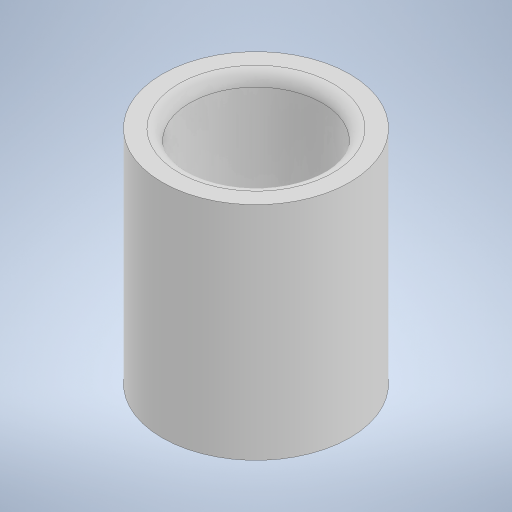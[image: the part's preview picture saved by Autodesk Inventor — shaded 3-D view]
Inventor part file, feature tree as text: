
AUTODESK INVENTOR PART (.ipt)
format: ipt  version: 2024.2 (Build 282272000, 272)  size: 531,456 bytes
history: native  units: in
note: dims shown in document units (in); Inventor stores cm internally (conversion verified against a paired STEP export)
features: extrude x1, fillet x1, sketch x1
ambient origin geometry x8: Origin, YZ Plane, XZ Plane, XY Plane, X Axis, Y Axis, Z Axis, Center Point
bodies: Solid1 (feature_tree)
feature tree (3):
  extrude  "Extrusion1"  Depth=0.05in
  fillet  "Fillet1"  Radius=1.0in
  sketch  "Sketch1"  dims[d0=0.597in d1=0.125in d2=1.0in d3=0.0in d4=0.05in]
